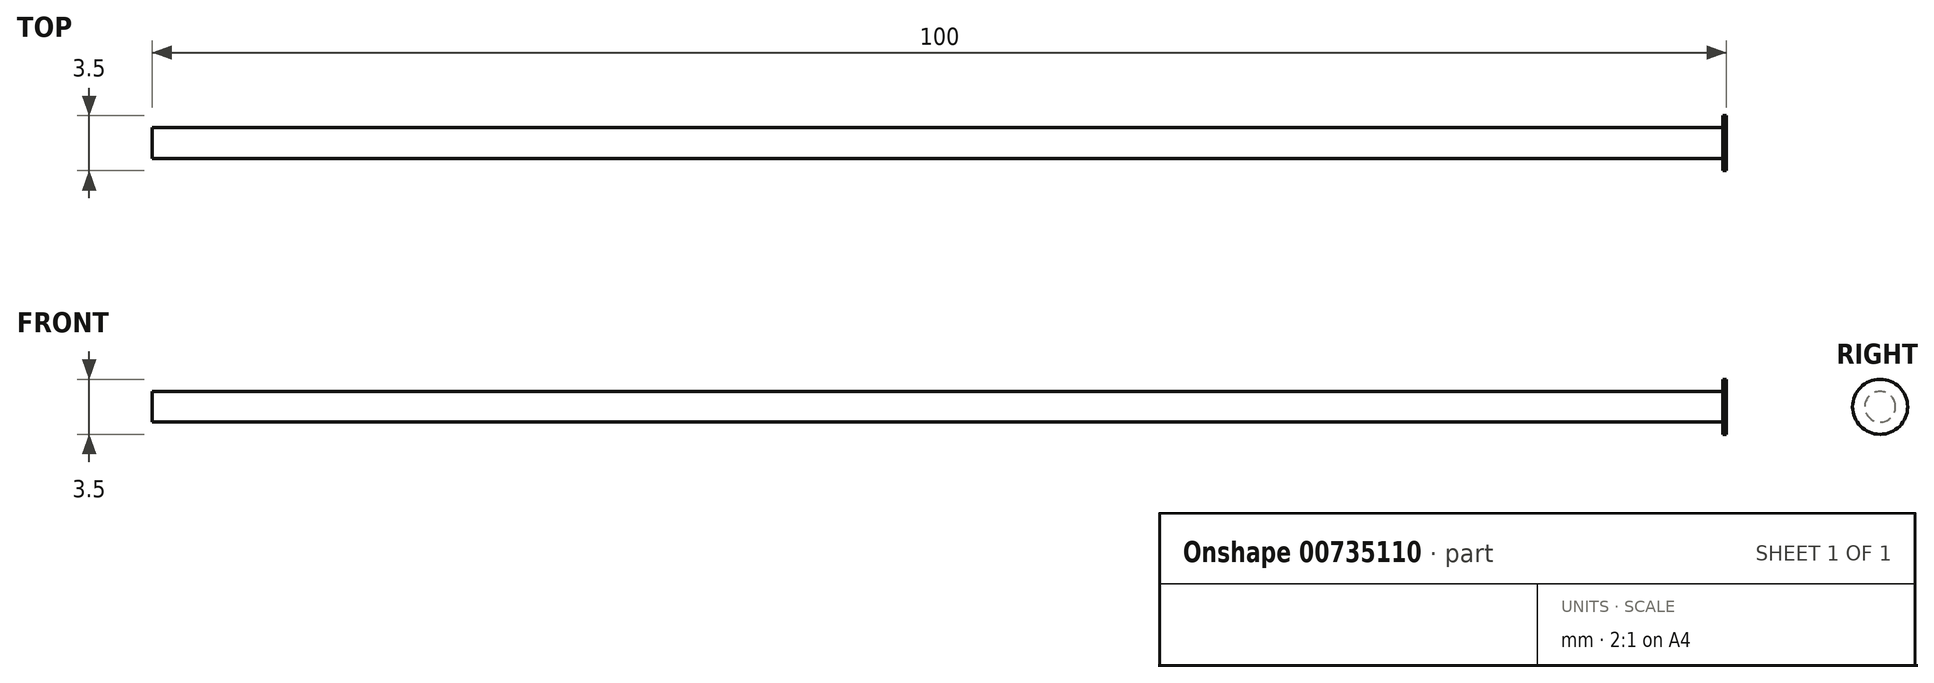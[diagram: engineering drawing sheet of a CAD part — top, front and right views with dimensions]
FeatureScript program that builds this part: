
annotation { "Feature Type Name" : "Feature", "Feature Type Description" : "" }
export const myFeature = defineFeature(function(context is Context, id is Id, definition is map)
    precondition{}
    {
        {
            var Q0;
            Q0=qCreatedBy(makeId("Right.planeOp"),FACE);
            var sketch = newSketch(context, id + "F0", { "sketchPlane" : qUnion([Q0])});
            skCircle(sketch, "E0", {"center": v(0, 0) * mm, "radius": 0.98 * mm});
            skSolve(sketch);
        }
        {
            var Q0;
            Q0 = qSketchRegion(id + "F0", true);
            extrude(context, id + "F1", {"entities" : qUnion([Q0]), "oppositeDirection" : true, "depth" : 100 * mm, "offsetDistance" : 25 * mm});
        }
        {
            var Q0;
            Q0=makeQuery(id+"F1.opExtrude","CAP_FACE",FACE,{"disambiguationData":[OSD([sQuery(id+"F0.wireOp",EDGE,"E0")])],"isStart":true});
            var sketch = newSketch(context, id + "F2", { "sketchPlane" : qUnion([Q0])});
            skCircle(sketch, "E1", {"center": v(0, 0) * mm, "radius": 1.75 * mm});
            skSolve(sketch);
        }
        {
            var Q0;
            Q0 = qSketchRegion(id + "F2", true);
            extrude(context, id + "F3", {"entities" : qUnion([Q0]), "operationType" : NewBodyOperationType.ADD, "oppositeDirection" : true, "depth" : 0.25 * mm, "offsetDistance" : 25 * mm});
        }
    });
